# Revit family: Gira_039003
name_source: partatom
category: Elektroinstallationen
revit_build: Autodesk Revit 2017 (Build: 20160225_1515(x64)
units: mm (PartAtom-declared; Revit-internal decimal feet)

## family parameters
Basisbauteil = Fläche
Beim Laden mit Abzugskörper schneiden = Nein
Bemaßung runder Anschluss = Durchmesser verwenden
Beschriftungsausrichtung beibehalten = Nein
Gemeinsam genutzt = Nein
Raumberechnungspunkt = Nein
Teiletyp = Normal

## types (2) — shared parameters
Acoustic signal = Ja
Adjustable differential = Nein
Analogue input = Nein
BIM = https://media.stage.bim.site und Tasten.rfa
Beschreibung = RTC 230V NC con. Sys55 PW,Room temperature controller 230 10 (4) A~ with NC contact,System 55,pure white glossy,Notes :,- For screw mounting only.,- Flat design.
Bus connection included = Nein
Bus system KNX = Ja
Bus system KNX radio = Nein
Bus system LON = Nein
Bus system Powernet = Nein
Bus system radio frequent = Nein
Colour = Clear white
Connection = Two-wire
Control characteristic = Other
Cooling = Nein
Data sheet = https://katalog.gira.de
Degree of protection (IP) = IP20
Explosion-proof = Nein
External sensor = Nein
GTIN = 4010337390039
HAN = 039003
Halogen free = Ja
Heating = Ja
Hersteller = Gira
Imprint/indication = Without imprint
Material = Other
Material quality = Other
Measuring range maximum value [m/s] = 30
Measuring range minimum value [m/s] = 5
Model = On/Off
Monitoring window/light outlet = Ja
Mounting method = Flush mounted (plaster)
Number of channels = 3
Operation = Turn
Other bus systems = None
Productwebsite = http://katalog.gira.de
RAL-number = 9010
RAL-number (akin) = 9010
Scannable symbol / barrier free = Nein
Sensor/feeler type = Other
Suitable for degree of protection (IP) = IP20
Suitable for touch sensor connector for bus system = Nein
Surface finishing = Not applicable
Surface protection = Other
Temperature readable = Nein
Thermal feedback = None
Transparent = Nein
Type of fastening = Clamp mounting
Type of power supply = 230 V AC
Typname = RTC 230/10 (4) A NC con. System 55 p.white
URL = https://www.gira.de
Utilization = Switch/push button
Vorgabe-Ansicht = 1219 mm
Weather station = Nein
With DCF77 = Nein
With display = Nein
With exchangeable lens/symbol = Nein
With heating = Nein
With label area = Nein
With receiver = Nein
With sound indicator = Nein
With tap water circuit = Nein

## per-type parameters (varying)
| type | Bauelement |
| Rocker set 3-g in.sp. System 55 clear/p.white | Sys55_Abdeckung_Schalten und Tasten |
| Sys55_Abdeckung_Schalten und Tasten |  |

## geometry (parser evidence)
native form markers: Sweep x6
no freeform markers — native parametric forms only
